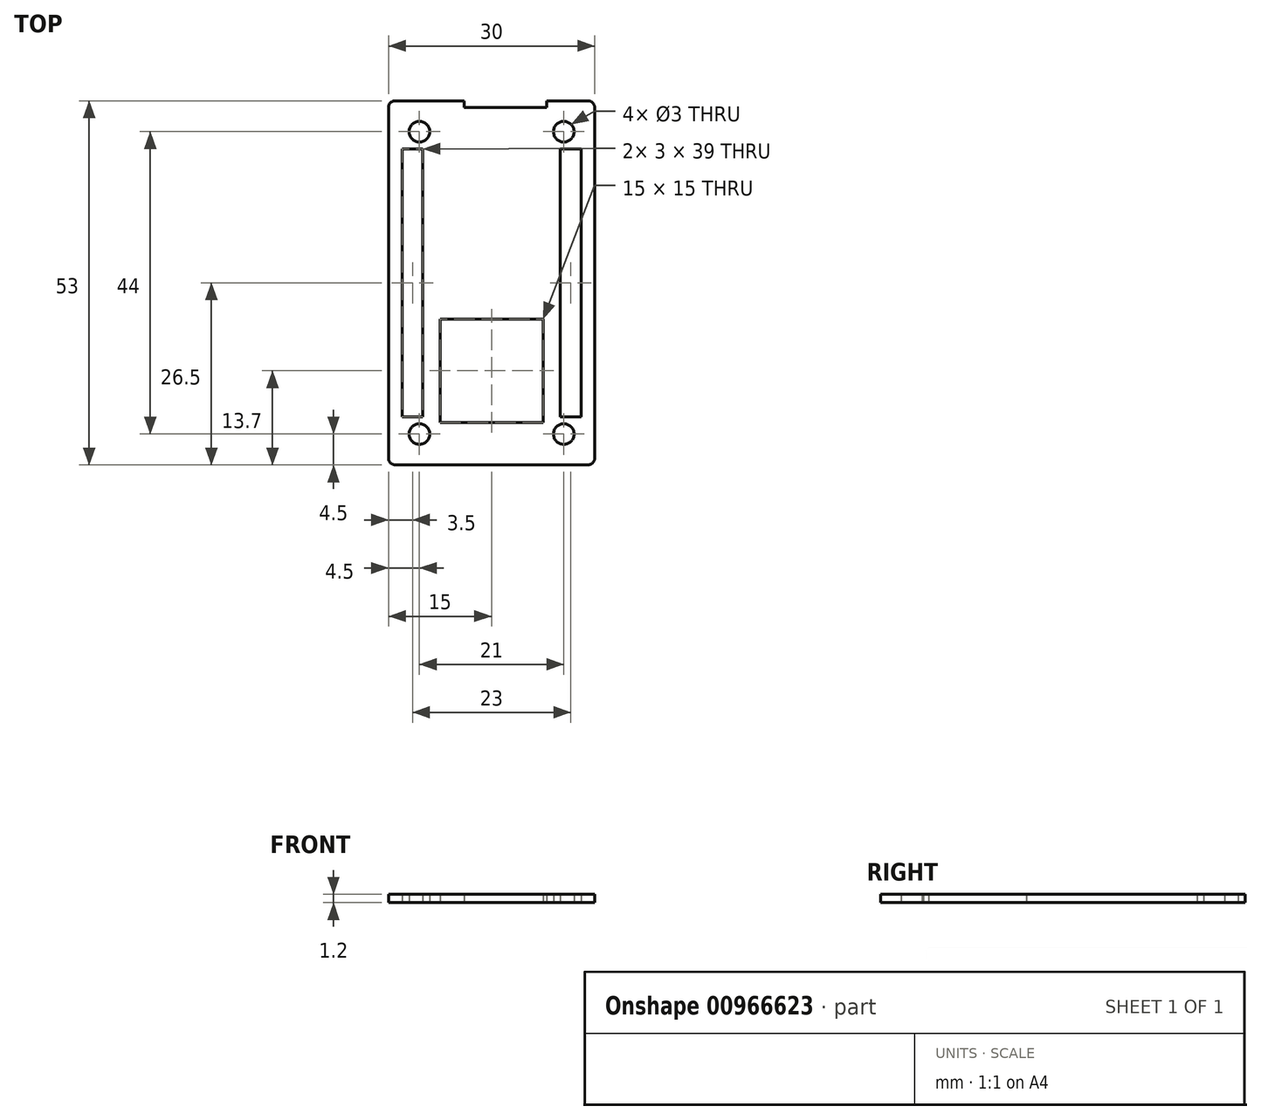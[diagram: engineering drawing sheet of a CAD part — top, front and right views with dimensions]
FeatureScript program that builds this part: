
annotation { "Feature Type Name" : "Feature", "Feature Type Description" : "" }
export const myFeature = defineFeature(function(context is Context, id is Id, definition is map)
    precondition{}
    {
        {
            var Q0;
            Q0=qCreatedBy(makeId("Top.planeOp"),FACE);
            var sketch = newSketch(context, id + "F0", { "sketchPlane" : qUnion([Q0])});
            skLineSegment(sketch, "E0.bottom", {"start": v(-12, 24.5) * mm, "end": v(12, 24.5) * mm});
            skLineSegment(sketch, "E0.top", {"start": v(-12, -24.5) * mm, "end": v(12, -24.5) * mm});
            skLineSegment(sketch, "E0.left", {"start": v(-13, 23.5) * mm, "end": v(-13, -23.5) * mm});
            skLineSegment(sketch, "E0.right", {"start": v(13, 23.5) * mm, "end": v(13, -23.5) * mm});
            skPoint(sketch, "E0.middle", {"position": v(0, 0) * mm});
            skLineSegment(sketch, "E1.0", {"start": v(-14, 26.5) * mm, "end": v(14, 26.5) * mm});
            skLineSegment(sketch, "E1.1", {"start": v(-15, 25.5) * mm, "end": v(-15, -25.5) * mm});
            skLineSegment(sketch, "E1.2", {"start": v(-14, -26.5) * mm, "end": v(14, -26.5) * mm});
            skLineSegment(sketch, "E1.3", {"start": v(15, 25.5) * mm, "end": v(15, -25.5) * mm});
            skPoint(sketch, "E2", {"position": v(0, 26.5) * mm});
            skPoint(sketch, "E3", {"position": v(0, 24.5) * mm});
            skLineSegment(sketch, "E4", {"start": v(0, 24.5) * mm, "end": v(4, 24.5) * mm});
            skLineSegment(sketch, "E5", {"start": v(0, 26.5) * mm, "end": v(4, 26.5) * mm});
            skLineSegment(sketch, "E6.MirrorCS", {"start": v(0, 24.5) * mm, "end": v(-4, 24.5) * mm});
            skLineSegment(sketch, "E7", {"start": v(0, 26.5) * mm, "end": v(-4, 26.5) * mm});
            skLineSegment(sketch, "E8", {"start": v(-4, 26.5) * mm, "end": v(-4, 24.5) * mm});
            skLineSegment(sketch, "E9", {"start": v(4, 26.5) * mm, "end": v(4, 24.5) * mm});
            skLineSegment(sketch, "E10.bottom", {"start": v(-4, 24.5) * mm, "end": v(4, 24.5) * mm});
            skLineSegment(sketch, "E10.top", {"start": v(-4, 20) * mm, "end": v(4, 20) * mm});
            skLineSegment(sketch, "E10.left", {"start": v(-4, 24.5) * mm, "end": v(-4, 20) * mm});
            skLineSegment(sketch, "E10.right", {"start": v(4, 24.5) * mm, "end": v(4, 20) * mm});
            skLineSegment(sketch, "E11.bottom", {"start": v(0, 26.5) * mm, "end": v(-8, 26.5) * mm});
            skLineSegment(sketch, "E11.top", {"start": v(0, 24.5) * mm, "end": v(-8, 24.5) * mm});
            skLineSegment(sketch, "E11.left", {"start": v(0, 26.5) * mm, "end": v(0, 24.5) * mm});
            skLineSegment(sketch, "E11.right", {"start": v(-8, 26.5) * mm, "end": v(-8, 24.5) * mm});
            skLineSegment(sketch, "E12.bottom", {"start": v(0, 26.5) * mm, "end": v(8, 26.5) * mm});
            skLineSegment(sketch, "E12.top", {"start": v(0, 24.5) * mm, "end": v(8, 24.5) * mm});
            skLineSegment(sketch, "E12.right", {"start": v(8, 26.5) * mm, "end": v(8, 24.5) * mm});
            skLineSegment(sketch, "E13", {"start": v(-8, 26.5) * mm, "end": v(-8, 25.5) * mm});
            skLineSegment(sketch, "E14", {"start": v(-8, 25.5) * mm, "end": v(8, 25.5) * mm});
            skPoint(sketch, "E15.visualSharp", {"position": v(-15, -26.5) * mm});
            skArc(sketch, "E15.filletArc", {"start": v(-15, -25.5) * mm, "mid": v(-14.7, -26.2) * mm, "end": v(-14, -26.5) * mm});
            skPoint(sketch, "E16.visualSharp", {"position": v(15, -26.5) * mm});
            skArc(sketch, "E16.filletArc", {"start": v(14, -26.5) * mm, "mid": v(14.7, -26.2) * mm, "end": v(15, -25.5) * mm});
            skPoint(sketch, "E17.visualSharp", {"position": v(-15, 26.5) * mm});
            skArc(sketch, "E17.filletArc", {"start": v(-14, 26.5) * mm, "mid": v(-14.7, 26.2) * mm, "end": v(-15, 25.5) * mm});
            skPoint(sketch, "E18.visualSharp", {"position": v(15, 26.5) * mm});
            skArc(sketch, "E18.filletArc", {"start": v(15, 25.5) * mm, "mid": v(14.7, 26.2) * mm, "end": v(14, 26.5) * mm});
            skPoint(sketch, "E19.visualSharp", {"position": v(13, 24.5) * mm});
            skArc(sketch, "E19.filletArc", {"start": v(13, 23.5) * mm, "mid": v(12.7, 24.2) * mm, "end": v(12, 24.5) * mm});
            skPoint(sketch, "E20.visualSharp", {"position": v(13, -24.5) * mm});
            skArc(sketch, "E20.filletArc", {"start": v(12, -24.5) * mm, "mid": v(12.7, -24.2) * mm, "end": v(13, -23.5) * mm});
            skPoint(sketch, "E21.visualSharp", {"position": v(-13, -24.5) * mm});
            skArc(sketch, "E21.filletArc", {"start": v(-13, -23.5) * mm, "mid": v(-12.7, -24.2) * mm, "end": v(-12, -24.5) * mm});
            skPoint(sketch, "E22.visualSharp", {"position": v(-13, 24.5) * mm});
            skArc(sketch, "E22.filletArc", {"start": v(-12, 24.5) * mm, "mid": v(-12.7, 24.2) * mm, "end": v(-13, 23.5) * mm});
            skLineSegment(sketch, "E23.bottom", {"start": v(-13, 24.5) * mm, "end": v(-10.5, 24.5) * mm});
            skLineSegment(sketch, "E23.top", {"start": v(-13, 22) * mm, "end": v(-10.5, 22) * mm});
            skLineSegment(sketch, "E23.left", {"start": v(-13, 24.5) * mm, "end": v(-13, 22) * mm});
            skLineSegment(sketch, "E23.right", {"start": v(-10.5, 24.5) * mm, "end": v(-10.5, 22) * mm});
            skLineSegment(sketch, "E24.MirrorCS", {"start": v(10.5, 24.5) * mm, "end": v(10.5, 22) * mm});
            skLineSegment(sketch, "E25.MirrorCS", {"start": v(13, 22) * mm, "end": v(10.5, 22) * mm});
            skLineSegment(sketch, "E26.MirrorCS", {"start": v(-13, -22) * mm, "end": v(-10.5, -22) * mm});
            skLineSegment(sketch, "E27.MirrorCS", {"start": v(-10.5, -24.5) * mm, "end": v(-10.5, -22) * mm});
            skLineSegment(sketch, "E28.MirrorCS", {"start": v(10.5, -24.5) * mm, "end": v(10.5, -22) * mm});
            skLineSegment(sketch, "E29.MirrorCS", {"start": v(13, -22) * mm, "end": v(10.5, -22) * mm});
            skCircle(sketch, "E30", {"center": v(-10.5, 22) * mm, "radius": 1.5 * mm});
            skCircle(sketch, "E31", {"center": v(10.5, 22) * mm, "radius": 1.5 * mm});
            skCircle(sketch, "E32", {"center": v(10.5, -22) * mm, "radius": 1.5 * mm});
            skCircle(sketch, "E33", {"center": v(-10.5, -22) * mm, "radius": 1.5 * mm});
            skPoint(sketch, "E34", {"position": v(10.5, 23.5) * mm});
            skLineSegment(sketch, "E35", {"start": v(10.5, 22) * mm, "end": v(10.5, 19.18) * mm});
            skLineSegment(sketch, "E36", {"start": v(-10.5, 22) * mm, "end": v(-10.5, 19.5) * mm});
            skLineSegment(sketch, "E37", {"start": v(10.5, -22) * mm, "end": v(10.5, -19.5) * mm});
            skLineSegment(sketch, "E38", {"start": v(-10.5, -22) * mm, "end": v(-10.5, -19.5) * mm});
            skLineSegment(sketch, "E39", {"start": v(-10.5, 19.5) * mm, "end": v(-10, 19.5) * mm});
            skLineSegment(sketch, "E40", {"start": v(10.5, 19.18) * mm, "end": v(10, 19.18) * mm});
            skLineSegment(sketch, "E41", {"start": v(10.5, -19.5) * mm, "end": v(10, -19.5) * mm});
            skLineSegment(sketch, "E42", {"start": v(-10.5, -19.5) * mm, "end": v(-10, -19.5) * mm});
            skLineSegment(sketch, "E43.bottom", {"start": v(-10, 19.5) * mm, "end": v(10, 19.5) * mm});
            skLineSegment(sketch, "E43.top", {"start": v(-10, -19.5) * mm, "end": v(10, -19.5) * mm});
            skLineSegment(sketch, "E43.left", {"start": v(-10, 19.5) * mm, "end": v(-10, -19.5) * mm});
            skLineSegment(sketch, "E43.right", {"start": v(10, 19.5) * mm, "end": v(10, -19.5) * mm});
            skLineSegment(sketch, "E44", {"start": v(-15, 19.5) * mm, "end": v(15, 19.5) * mm});
            skLineSegment(sketch, "E45", {"start": v(15, -19.5) * mm, "end": v(-15, -19.5) * mm});
            skLineSegment(sketch, "E46", {"start": v(10, -19.5) * mm, "end": v(10, -20.3) * mm});
            skLineSegment(sketch, "E47", {"start": v(15, -20.3) * mm, "end": v(-15, -20.3) * mm});
            skPoint(sketch, "E48", {"position": v(0, -20.3) * mm});
            skLineSegment(sketch, "E49", {"start": v(0, -20.3) * mm, "end": v(0, -12.8) * mm});
            skLineSegment(sketch, "E50.bottom", {"start": v(-7.5, -5.3) * mm, "end": v(7.5, -5.3) * mm});
            skLineSegment(sketch, "E50.top", {"start": v(-7.5, -20.3) * mm, "end": v(7.5, -20.3) * mm});
            skLineSegment(sketch, "E50.left", {"start": v(-7.5, -5.3) * mm, "end": v(-7.5, -20.3) * mm});
            skLineSegment(sketch, "E50.right", {"start": v(7.5, -5.3) * mm, "end": v(7.5, -20.3) * mm});
            skPoint(sketch, "E50.middle", {"position": v(0, -12.8) * mm});
            skSolve(sketch);
        }
        {
            var Q0;
            {var subQ0=sQuery(id+"F0.wireOp",EDGE,"E44");var subQ1=sQuery(id+"F0.wireOp",EDGE,"E0.left");var subQ2=makeQuery(id+"F0.imprint","INTERSECT",VERTEX,{"derivedFrom":[subQ1,subQ0]});Q0=makeQuery(id+"F0.imprint","IMPRINT",FACE,{"disambiguationData":[TD([[makeQuery(id+"F0.imprint","IMPRINT",EDGE,{"disambiguationData":[TD([[subQ2,-1.0]])],"derivedFrom":subQ1}),-1.0]])]});}
            var Q1;
            {var subQ0=sQuery(id+"F0.wireOp",EDGE,"E44");var subQ1=sQuery(id+"F0.wireOp",EDGE,"E0.right");var subQ2=makeQuery(id+"F0.imprint","INTERSECT",VERTEX,{"derivedFrom":[subQ1,subQ0]});Q1=makeQuery(id+"F0.imprint","IMPRINT",FACE,{"disambiguationData":[TD([[makeQuery(id+"F0.imprint","IMPRINT",EDGE,{"disambiguationData":[TD([[subQ2,-1.0]])],"derivedFrom":subQ1}),1.0]])]});}
            var Q2;
            {var subQ4=sQuery(id+"F0.wireOp",EDGE,"E43.left");Q2=makeQuery(id+"F0.imprint","IMPRINT",FACE,{"disambiguationData":[TD([[makeQuery(id+"F0.imprint","IMPRINT",EDGE,{"derivedFrom":subQ4}),1.0]])]});}
            var Q3;
            {var subQ5=sQuery(id+"F0.wireOp",EDGE,"E11.right");Q3=makeQuery(id+"F0.imprint","IMPRINT",FACE,{"disambiguationData":[TD([[makeQuery(id+"F0.imprint","IMPRINT",EDGE,{"derivedFrom":subQ5}),-1.0]])]});}
            var Q4;
            {var subQ3=sQuery(id+"F0.wireOp",EDGE,"E30");var subQ5=sQuery(id+"F0.wireOp",EDGE,"E23.top");var subQ6=makeQuery(id+"F0.imprint","INTERSECT",VERTEX,{"derivedFrom":[subQ5,subQ3]});Q4=makeQuery(id+"F0.imprint","IMPRINT",FACE,{"disambiguationData":[TD([[makeQuery(id+"F0.imprint","IMPRINT",EDGE,{"disambiguationData":[TD([[subQ6,-1.0]])],"derivedFrom":subQ3}),-1.0]])]});}
            var Q5;
            Q5=makeQuery(id+"F0.imprint","IMPRINT",FACE,{"disambiguationData":[TD([[makeQuery(id+"F0.imprint","IMPRINT",EDGE,{"derivedFrom":sQuery(id+"F0.wireOp",EDGE,"E10.top")}),-1.0]])]});
            var Q6;
            Q6=makeQuery(id+"F0.imprint","IMPRINT",FACE,{"disambiguationData":[TD([[makeQuery(id+"F0.imprint","IMPRINT",EDGE,{"derivedFrom":sQuery(id+"F0.wireOp",EDGE,"E10.top")}),1.0]])]});
            var Q7;
            {var subQ5=sQuery(id+"F0.wireOp",EDGE,"E25.MirrorCS");var subQ7=sQuery(id+"F0.wireOp",EDGE,"E0.right");var subQ8=makeQuery(id+"F0.imprint","INTERSECT",VERTEX,{"derivedFrom":[subQ7,subQ5]});Q7=makeQuery(id+"F0.imprint","IMPRINT",FACE,{"disambiguationData":[TD([[makeQuery(id+"F0.imprint","IMPRINT",EDGE,{"disambiguationData":[TD([[subQ8,-1.0]])],"derivedFrom":subQ7}),-1.0]])]});}
            var Q8;
            {var subQ0=sQuery(id+"F0.wireOp",EDGE,"E18.filletArc");Q8=makeQuery(id+"F0.imprint","IMPRINT",FACE,{"disambiguationData":[TD([[makeQuery(id+"F0.imprint","IMPRINT",EDGE,{"derivedFrom":subQ0}),1.0]])]});}
            var Q9;
            Q9=makeQuery(id+"F0.imprint","IMPRINT",FACE,{"disambiguationData":[TD([[makeQuery(id+"F0.imprint","IMPRINT",EDGE,{"derivedFrom":sQuery(id+"F0.wireOp",EDGE,"E1.2")}),1.0]])]});
            var Q10;
            {var subQ1=sQuery(id+"F0.wireOp",EDGE,"E0.top");var subQ9=sQuery(id+"F0.wireOp",EDGE,"E27.MirrorCS");var subQ10=makeQuery(id+"F0.imprint","INTERSECT",VERTEX,{"derivedFrom":[subQ1,subQ9]});Q10=makeQuery(id+"F0.imprint","IMPRINT",FACE,{"disambiguationData":[TD([[makeQuery(id+"F0.imprint","IMPRINT",EDGE,{"disambiguationData":[TD([[subQ10,-1.0]])],"derivedFrom":subQ1}),1.0]])]});}
            var Q11;
            {var subQ5=sQuery(id+"F0.wireOp",EDGE,"E26.MirrorCS");var subQ7=sQuery(id+"F0.wireOp",EDGE,"E0.left");var subQ8=makeQuery(id+"F0.imprint","INTERSECT",VERTEX,{"derivedFrom":[subQ7,subQ5]});Q11=makeQuery(id+"F0.imprint","IMPRINT",FACE,{"disambiguationData":[TD([[makeQuery(id+"F0.imprint","IMPRINT",EDGE,{"disambiguationData":[TD([[subQ8,1.0]])],"derivedFrom":subQ7}),1.0]])]});}
            var Q12;
            {var subQ0=sQuery(id+"F0.wireOp",EDGE,"E21.filletArc");Q12=makeQuery(id+"F0.imprint","IMPRINT",FACE,{"disambiguationData":[TD([[makeQuery(id+"F0.imprint","IMPRINT",EDGE,{"derivedFrom":subQ0}),1.0]])]});}
            var Q13;
            {var subQ5=sQuery(id+"F0.wireOp",EDGE,"E29.MirrorCS");var subQ6=sQuery(id+"F0.wireOp",EDGE,"E0.right");var subQ7=makeQuery(id+"F0.imprint","INTERSECT",VERTEX,{"derivedFrom":[subQ6,subQ5]});Q13=makeQuery(id+"F0.imprint","IMPRINT",FACE,{"disambiguationData":[TD([[makeQuery(id+"F0.imprint","IMPRINT",EDGE,{"disambiguationData":[TD([[subQ7,1.0]])],"derivedFrom":subQ6}),-1.0]])]});}
            var Q14;
            {var subQ5=sQuery(id+"F0.wireOp",EDGE,"E20.filletArc");Q14=makeQuery(id+"F0.imprint","IMPRINT",FACE,{"disambiguationData":[TD([[makeQuery(id+"F0.imprint","IMPRINT",EDGE,{"derivedFrom":subQ5}),1.0]])]});}
            var Q15;
            {var subQ3=sQuery(id+"F0.wireOp",EDGE,"E22.filletArc");Q15=makeQuery(id+"F0.imprint","IMPRINT",FACE,{"disambiguationData":[TD([[makeQuery(id+"F0.imprint","IMPRINT",EDGE,{"derivedFrom":subQ3}),1.0]])]});}
            var Q16;
            {var subQ0=sQuery(id+"F0.wireOp",EDGE,"E19.filletArc");Q16=makeQuery(id+"F0.imprint","IMPRINT",FACE,{"disambiguationData":[TD([[makeQuery(id+"F0.imprint","IMPRINT",EDGE,{"derivedFrom":subQ0}),1.0]])]});}
            var Q17;
            {var subQ0=sQuery(id+"F0.wireOp",EDGE,"E22.filletArc");Q17=makeQuery(id+"F0.imprint","IMPRINT",FACE,{"disambiguationData":[TD([[makeQuery(id+"F0.imprint","IMPRINT",EDGE,{"derivedFrom":subQ0}),-1.0]])]});}
            var Q18;
            {var subQ0=sQuery(id+"F0.wireOp",EDGE,"E49");var subQ1=sQuery(id+"F0.wireOp",EDGE,"E45");var subQ2=makeQuery(id+"F0.imprint","INTERSECT",VERTEX,{"derivedFrom":[subQ1,subQ0]});Q18=makeQuery(id+"F0.imprint","IMPRINT",FACE,{"disambiguationData":[TD([[makeQuery(id+"F0.imprint","IMPRINT",EDGE,{"disambiguationData":[TD([[subQ2,-1.0]])],"derivedFrom":subQ1}),1.0]])]});}
            var Q19;
            {var subQ0=sQuery(id+"F0.wireOp",EDGE,"E49");var subQ1=sQuery(id+"F0.wireOp",EDGE,"E45");var subQ2=makeQuery(id+"F0.imprint","INTERSECT",VERTEX,{"derivedFrom":[subQ1,subQ0]});Q19=makeQuery(id+"F0.imprint","IMPRINT",FACE,{"disambiguationData":[TD([[makeQuery(id+"F0.imprint","IMPRINT",EDGE,{"disambiguationData":[TD([[subQ2,1.0]])],"derivedFrom":subQ1}),1.0]])]});}
            var Q20;
            {var subQ0=sQuery(id+"F0.wireOp",EDGE,"E46");Q20=makeQuery(id+"F0.imprint","IMPRINT",FACE,{"disambiguationData":[TD([[makeQuery(id+"F0.imprint","IMPRINT",EDGE,{"derivedFrom":subQ0}),-1.0]])]});}
            var Q21;
            {var subQ0=sQuery(id+"F0.wireOp",EDGE,"E45");var subQ1=sQuery(id+"F0.wireOp",EDGE,"E0.right");var subQ2=makeQuery(id+"F0.imprint","INTERSECT",VERTEX,{"derivedFrom":[subQ1,subQ0]});Q21=makeQuery(id+"F0.imprint","IMPRINT",FACE,{"disambiguationData":[TD([[makeQuery(id+"F0.imprint","IMPRINT",EDGE,{"disambiguationData":[TD([[subQ2,-1.0]])],"derivedFrom":subQ1}),-1.0]])]});}
            var Q22;
            {var subQ0=sQuery(id+"F0.wireOp",EDGE,"E45");var subQ1=sQuery(id+"F0.wireOp",EDGE,"E0.right");var subQ2=makeQuery(id+"F0.imprint","INTERSECT",VERTEX,{"derivedFrom":[subQ1,subQ0]});Q22=makeQuery(id+"F0.imprint","IMPRINT",FACE,{"disambiguationData":[TD([[makeQuery(id+"F0.imprint","IMPRINT",EDGE,{"disambiguationData":[TD([[subQ2,-1.0]])],"derivedFrom":subQ1}),1.0]])]});}
            var Q23;
            {var subQ5=sQuery(id+"F0.wireOp",EDGE,"E46");Q23=makeQuery(id+"F0.imprint","IMPRINT",FACE,{"disambiguationData":[TD([[makeQuery(id+"F0.imprint","IMPRINT",EDGE,{"derivedFrom":subQ5}),1.0]])]});}
            var Q24;
            {var subQ3=sQuery(id+"F0.wireOp",EDGE,"E38");var subQ5=sQuery(id+"F0.wireOp",EDGE,"E45");var subQ6=makeQuery(id+"F0.imprint","INTERSECT",VERTEX,{"derivedFrom":[subQ3,subQ5]});Q24=makeQuery(id+"F0.imprint","IMPRINT",FACE,{"disambiguationData":[TD([[makeQuery(id+"F0.imprint","IMPRINT",EDGE,{"disambiguationData":[TD([[subQ6,1.0]])],"derivedFrom":subQ3}),-1.0]])]});}
            var Q25;
            {var subQ0=sQuery(id+"F0.wireOp",EDGE,"E45");var subQ1=sQuery(id+"F0.wireOp",EDGE,"E0.left");var subQ2=makeQuery(id+"F0.imprint","INTERSECT",VERTEX,{"derivedFrom":[subQ1,subQ0]});Q25=makeQuery(id+"F0.imprint","IMPRINT",FACE,{"disambiguationData":[TD([[makeQuery(id+"F0.imprint","IMPRINT",EDGE,{"disambiguationData":[TD([[subQ2,-1.0]])],"derivedFrom":subQ1}),1.0]])]});}
            var Q26;
            {var subQ0=sQuery(id+"F0.wireOp",EDGE,"E45");var subQ1=sQuery(id+"F0.wireOp",EDGE,"E0.left");var subQ2=makeQuery(id+"F0.imprint","INTERSECT",VERTEX,{"derivedFrom":[subQ1,subQ0]});Q26=makeQuery(id+"F0.imprint","IMPRINT",FACE,{"disambiguationData":[TD([[makeQuery(id+"F0.imprint","IMPRINT",EDGE,{"disambiguationData":[TD([[subQ2,-1.0]])],"derivedFrom":subQ1}),-1.0]])]});}
            var Q27;
            {var subQ5=sQuery(id+"F0.wireOp",EDGE,"E11.right");Q27=makeQuery(id+"F0.imprint","IMPRINT",FACE,{"disambiguationData":[TD([[makeQuery(id+"F0.imprint","IMPRINT",EDGE,{"derivedFrom":subQ5}),1.0]])]});}
            var Q28;
            {var subQ1=sQuery(id+"F0.wireOp",EDGE,"E8");var subQ3=sQuery(id+"F0.wireOp",EDGE,"E14");var subQ4=makeQuery(id+"F0.imprint","INTERSECT",VERTEX,{"derivedFrom":[subQ1,subQ3]});Q28=makeQuery(id+"F0.imprint","IMPRINT",FACE,{"disambiguationData":[TD([[makeQuery(id+"F0.imprint","IMPRINT",EDGE,{"disambiguationData":[TD([[subQ4,-1.0]])],"derivedFrom":subQ3}),-1.0]])]});}
            var Q29;
            {var subQ1=sQuery(id+"F0.wireOp",EDGE,"E9");var subQ3=sQuery(id+"F0.wireOp",EDGE,"E14");var subQ4=makeQuery(id+"F0.imprint","INTERSECT",VERTEX,{"derivedFrom":[subQ1,subQ3]});Q29=makeQuery(id+"F0.imprint","IMPRINT",FACE,{"disambiguationData":[TD([[makeQuery(id+"F0.imprint","IMPRINT",EDGE,{"disambiguationData":[TD([[subQ4,1.0]])],"derivedFrom":subQ3}),-1.0]])]});}
            var Q30;
            {var subQ3=sQuery(id+"F0.wireOp",EDGE,"E14");var subQ5=sQuery(id+"F0.wireOp",EDGE,"E12.right");var subQ7=makeQuery(id+"F0.imprint","INTERSECT",VERTEX,{"derivedFrom":[subQ5,subQ3]});Q30=makeQuery(id+"F0.imprint","IMPRINT",FACE,{"disambiguationData":[TD([[makeQuery(id+"F0.imprint","IMPRINT",EDGE,{"disambiguationData":[TD([[subQ7,1.0]])],"derivedFrom":subQ3}),-1.0]])]});}
            extrude(context, id + "F1", {"entities" : qUnion([Q0, Q1, Q2, Q3, Q4, Q5, Q6, Q7, Q8, Q9, Q10, Q11, Q12, Q13, Q14, Q15, Q16, Q17, Q18, Q19, Q20, Q21, Q22, Q23, Q24, Q25, Q26, Q27, Q28, Q29, Q30]), "depth" : 1.2 * mm, "offsetDistance" : 25 * mm});
        }
    });
